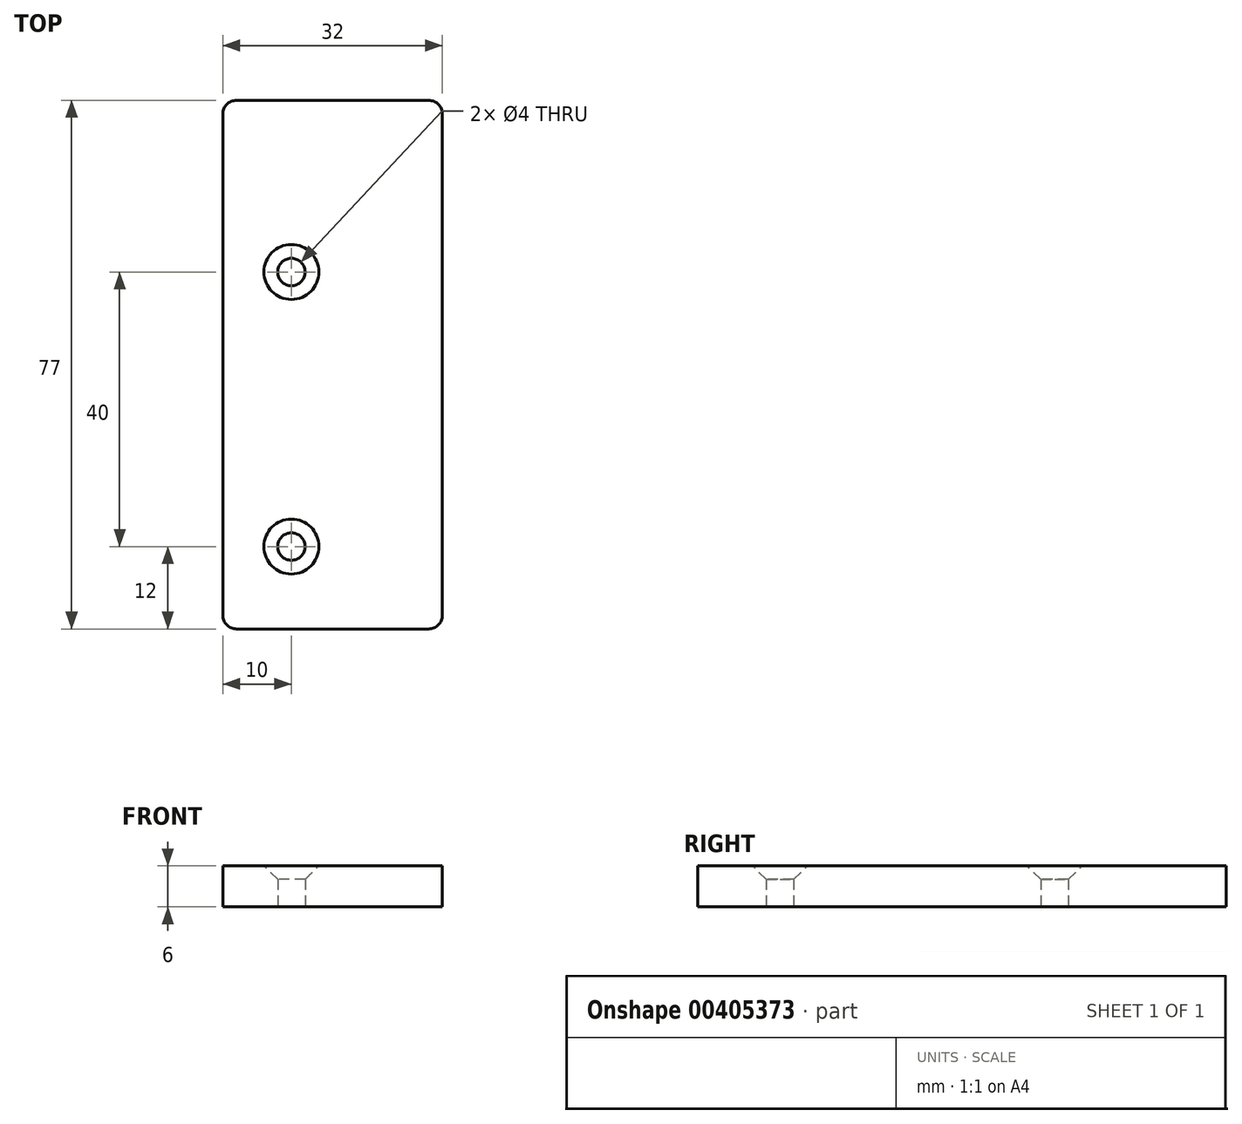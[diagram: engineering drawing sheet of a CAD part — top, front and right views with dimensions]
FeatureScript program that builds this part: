
annotation { "Feature Type Name" : "Feature", "Feature Type Description" : "" }
export const myFeature = defineFeature(function(context is Context, id is Id, definition is map)
    precondition{}
    {
        {
            var Q0;
            Q0=qCreatedBy(makeId("Top.planeOp"),FACE);
            var sketch = newSketch(context, id + "F0", { "sketchPlane" : qUnion([Q0])});
            skLineSegment(sketch, "E0.bottom", {"start": v(-16, 38.5) * mm, "end": v(16, 38.5) * mm});
            skLineSegment(sketch, "E0.top", {"start": v(-16, -38.5) * mm, "end": v(16, -38.5) * mm});
            skLineSegment(sketch, "E0.left", {"start": v(-16, 38.5) * mm, "end": v(-16, -38.5) * mm});
            skLineSegment(sketch, "E0.right", {"start": v(16, 38.5) * mm, "end": v(16, -38.5) * mm});
            skPoint(sketch, "E0.middle", {"position": v(0, 0) * mm});
            skCircle(sketch, "E1", {"center": v(-6, 13.5) * mm, "radius": 2 * mm});
            skCircle(sketch, "E2", {"center": v(-6, -26.5) * mm, "radius": 2 * mm});
            skSolve(sketch);
        }
        {
            var Q0;
            Q0=makeQuery(id+"F0.imprint","IMPRINT",FACE,{"disambiguationData":[TD([[makeQuery(id+"F0.imprint","IMPRINT",EDGE,{"derivedFrom":sQuery(id+"F0.wireOp",EDGE,"E0.bottom")}),-1.0]])]});
            extrude(context, id + "F1", {"entities" : qUnion([Q0]), "depth" : 6 * mm});
        }
        {
            var Q0;
            Q0=makeQuery(id+"F1.opExtrude","SWEPT_EDGE",EDGE,{"disambiguationData":[OSD([sQuery(id+"F0.wireOp",EDGE,"E0.bottom"),sQuery(id+"F0.wireOp",EDGE,"E0.left")])]});
            var Q1;
            Q1=makeQuery(id+"F1.opExtrude","SWEPT_EDGE",EDGE,{"disambiguationData":[OSD([sQuery(id+"F0.wireOp",EDGE,"E0.bottom"),sQuery(id+"F0.wireOp",EDGE,"E0.right")])]});
            var Q2;
            Q2=makeQuery(id+"F1.opExtrude","SWEPT_EDGE",EDGE,{"disambiguationData":[OSD([sQuery(id+"F0.wireOp",EDGE,"E0.top"),sQuery(id+"F0.wireOp",EDGE,"E0.right")])]});
            var Q3;
            Q3=makeQuery(id+"F1.opExtrude","SWEPT_EDGE",EDGE,{"disambiguationData":[OSD([sQuery(id+"F0.wireOp",EDGE,"E0.top"),sQuery(id+"F0.wireOp",EDGE,"E0.left")])]});
            fillet(context, id + "F2", {"entities" : qUnion([Q0, Q1, Q2, Q3]), "radius" : 2 * mm, "tangentPropagation" : true, "allowEdgeOverflow" : false});
        }
        {
            var Q0;
            Q0=makeQuery(id+"F1.opExtrude","CAP_FACE",FACE,{"disambiguationData":[OSD([sQuery(id+"F0.wireOp",EDGE,"E0.bottom"),sQuery(id+"F0.wireOp",EDGE,"E0.top"),sQuery(id+"F0.wireOp",EDGE,"E0.left"),sQuery(id+"F0.wireOp",EDGE,"E0.right"),sQuery(id+"F0.wireOp",EDGE,"E1"),sQuery(id+"F0.wireOp",EDGE,"E2")])],"isStart":false});
            var sketch = newSketch(context, id + "F3", { "sketchPlane" : qUnion([Q0])});
            skPoint(sketch, "E3", {"position": v(-6, 13.5) * mm});
            skPoint(sketch, "E4", {"position": v(-6, -26.5) * mm});
            skSolve(sketch);
        }
        {
            var Q0;
            Q0=sQuery(id+"F3.wireOp",VERTEX,"E3");
            var Q1;
            Q1=sQuery(id+"F3.wireOp",VERTEX,"E4");
            var Q2;
            Q2=makeQuery(id+"F1.opExtrude","SWEPT_BODY",BODY,{"disambiguationData":[OSD([sQuery(id+"F0.wireOp",EDGE,"E0.bottom"),sQuery(id+"F0.wireOp",EDGE,"E0.top"),sQuery(id+"F0.wireOp",EDGE,"E0.left"),sQuery(id+"F0.wireOp",EDGE,"E0.right"),sQuery(id+"F0.wireOp",EDGE,"E1"),sQuery(id+"F0.wireOp",EDGE,"E2")])]});
            hole(context, id + "F4", {"style" : HoleStyle.C_SINK, "endStyle" : HoleEndStyle.BLIND, "holeDiameter" : 4 * mm, "cSinkDiameter" : 8 * mm, "cSinkAngle" : 90 * degree, "holeDepth" : 10 * mm, "tappedDepth" : 12 * mm, "tapClearance" : 3, "locations" : qUnion([Q0, Q1]), "scope" : qUnion([Q2])});
        }
    });
